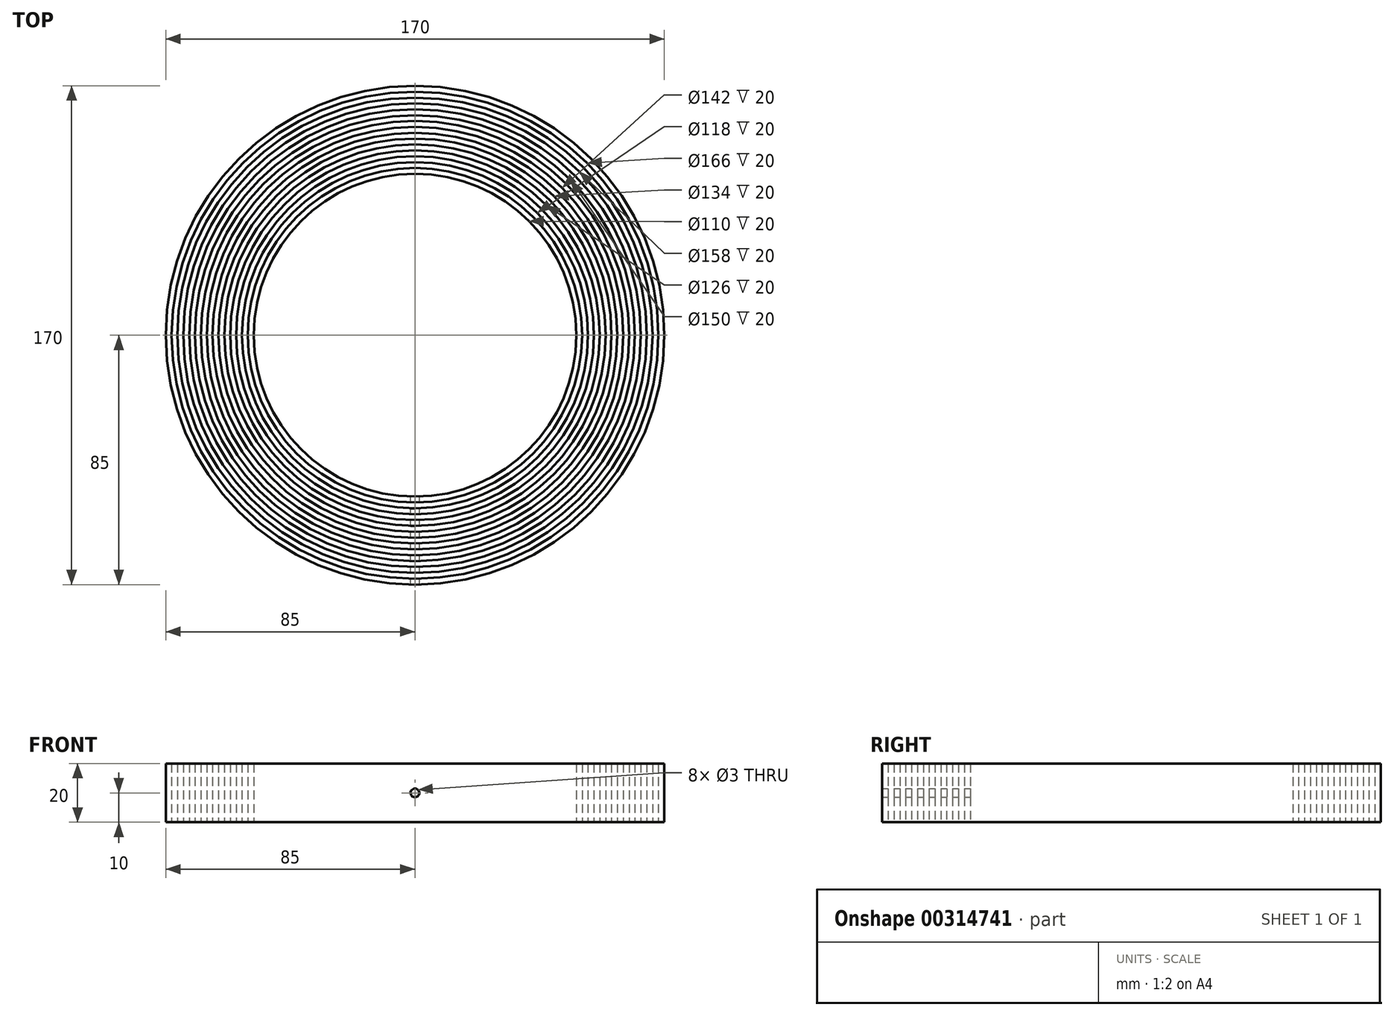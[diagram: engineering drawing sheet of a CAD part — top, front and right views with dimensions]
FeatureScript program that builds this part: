
annotation { "Feature Type Name" : "Feature", "Feature Type Description" : "" }
export const myFeature = defineFeature(function(context is Context, id is Id, definition is map)
    precondition{}
    {
        {
            var Q0;
            Q0=qCreatedBy(makeId("Top.planeOp"),FACE);
            var sketch = newSketch(context, id + "F0", { "sketchPlane" : qUnion([Q0])});
            skCircle(sketch, "E0", {"center": v(0, 0) * mm, "radius": 85 * mm});
            skCircle(sketch, "E1.0", {"center": v(0, 0) * mm, "radius": 83 * mm});
            skCircle(sketch, "E2.0", {"center": v(0, 0) * mm, "radius": 81 * mm});
            skCircle(sketch, "E3.0", {"center": v(0, 0) * mm, "radius": 79 * mm});
            skCircle(sketch, "E4.0", {"center": v(0, 0) * mm, "radius": 77 * mm});
            skCircle(sketch, "E5.0", {"center": v(0, 0) * mm, "radius": 75 * mm});
            skCircle(sketch, "E6.0", {"center": v(0, 0) * mm, "radius": 73 * mm});
            skCircle(sketch, "E7.0", {"center": v(0, 0) * mm, "radius": 71 * mm});
            skCircle(sketch, "E8.0", {"center": v(0, 0) * mm, "radius": 69 * mm});
            skCircle(sketch, "E9.0", {"center": v(0, 0) * mm, "radius": 67 * mm});
            skCircle(sketch, "E10.0", {"center": v(0, 0) * mm, "radius": 65 * mm});
            skCircle(sketch, "E11.0", {"center": v(0, 0) * mm, "radius": 63 * mm});
            skCircle(sketch, "E12.0", {"center": v(0, 0) * mm, "radius": 61 * mm});
            skCircle(sketch, "E13.0", {"center": v(0, 0) * mm, "radius": 59 * mm});
            skCircle(sketch, "E14.0", {"center": v(0, 0) * mm, "radius": 57 * mm});
            skCircle(sketch, "E15.0", {"center": v(0, 0) * mm, "radius": 55 * mm});
            skSolve(sketch);
        }
        {
            var Q0;
            Q0=makeQuery(id+"F0.imprint","IMPRINT",FACE,{"disambiguationData":[TD([[makeQuery(id+"F0.imprint","IMPRINT",EDGE,{"derivedFrom":sQuery(id+"F0.wireOp",EDGE,"E0")}),1.0]])]});
            var Q1;
            Q1=makeQuery(id+"F0.imprint","IMPRINT",FACE,{"disambiguationData":[TD([[makeQuery(id+"F0.imprint","IMPRINT",EDGE,{"derivedFrom":sQuery(id+"F0.wireOp",EDGE,"E2.0")}),1.0]])]});
            var Q2;
            Q2=makeQuery(id+"F0.imprint","IMPRINT",FACE,{"disambiguationData":[TD([[makeQuery(id+"F0.imprint","IMPRINT",EDGE,{"derivedFrom":sQuery(id+"F0.wireOp",EDGE,"E4.0")}),1.0]])]});
            var Q3;
            Q3=makeQuery(id+"F0.imprint","IMPRINT",FACE,{"disambiguationData":[TD([[makeQuery(id+"F0.imprint","IMPRINT",EDGE,{"derivedFrom":sQuery(id+"F0.wireOp",EDGE,"E6.0")}),1.0]])]});
            var Q4;
            Q4=makeQuery(id+"F0.imprint","IMPRINT",FACE,{"disambiguationData":[TD([[makeQuery(id+"F0.imprint","IMPRINT",EDGE,{"derivedFrom":sQuery(id+"F0.wireOp",EDGE,"E8.0")}),1.0]])]});
            var Q5;
            Q5=makeQuery(id+"F0.imprint","IMPRINT",FACE,{"disambiguationData":[TD([[makeQuery(id+"F0.imprint","IMPRINT",EDGE,{"derivedFrom":sQuery(id+"F0.wireOp",EDGE,"E10.0")}),1.0]])]});
            var Q6;
            Q6=makeQuery(id+"F0.imprint","IMPRINT",FACE,{"disambiguationData":[TD([[makeQuery(id+"F0.imprint","IMPRINT",EDGE,{"derivedFrom":sQuery(id+"F0.wireOp",EDGE,"E12.0")}),1.0]])]});
            var Q7;
            Q7=makeQuery(id+"F0.imprint","IMPRINT",FACE,{"disambiguationData":[TD([[makeQuery(id+"F0.imprint","IMPRINT",EDGE,{"derivedFrom":sQuery(id+"F0.wireOp",EDGE,"E14.0")}),1.0]])]});
            extrude(context, id + "F1", {"entities" : qUnion([Q0, Q1, Q2, Q3, Q4, Q5, Q6, Q7]), "depth" : 20 * mm});
        }
        {
            var Q0;
            Q0=qCreatedBy(makeId("Front.planeOp"),FACE);
            var sketch = newSketch(context, id + "F2", { "sketchPlane" : qUnion([Q0])});
            skCircle(sketch, "E16", {"center": v(0, 10) * mm, "radius": 1.5 * mm});
            skSolve(sketch);
        }
        {
            var Q0;
            Q0=sQuery(id+"F2.wireOp",VERTEX,"E16.center");
            var Q1;
            Q1=makeQuery(id+"F1.opExtrude","SWEPT_BODY",BODY,{"disambiguationData":[OSD([sQuery(id+"F0.wireOp",EDGE,"E0"),sQuery(id+"F0.wireOp",EDGE,"E1.0")])]});
            var Q2;
            Q2=makeQuery(id+"F1.opExtrude","SWEPT_BODY",BODY,{"disambiguationData":[OSD([sQuery(id+"F0.wireOp",EDGE,"E2.0"),sQuery(id+"F0.wireOp",EDGE,"E3.0")])]});
            var Q3;
            Q3=makeQuery(id+"F1.opExtrude","SWEPT_BODY",BODY,{"disambiguationData":[OSD([sQuery(id+"F0.wireOp",EDGE,"E4.0"),sQuery(id+"F0.wireOp",EDGE,"E5.0")])]});
            var Q4;
            Q4=makeQuery(id+"F1.opExtrude","SWEPT_BODY",BODY,{"disambiguationData":[OSD([sQuery(id+"F0.wireOp",EDGE,"E6.0"),sQuery(id+"F0.wireOp",EDGE,"E7.0")])]});
            var Q5;
            Q5=makeQuery(id+"F1.opExtrude","SWEPT_BODY",BODY,{"disambiguationData":[OSD([sQuery(id+"F0.wireOp",EDGE,"E8.0"),sQuery(id+"F0.wireOp",EDGE,"E9.0")])]});
            var Q6;
            Q6=makeQuery(id+"F1.opExtrude","SWEPT_BODY",BODY,{"disambiguationData":[OSD([sQuery(id+"F0.wireOp",EDGE,"E10.0"),sQuery(id+"F0.wireOp",EDGE,"E11.0")])]});
            var Q7;
            Q7=makeQuery(id+"F1.opExtrude","SWEPT_BODY",BODY,{"disambiguationData":[OSD([sQuery(id+"F0.wireOp",EDGE,"E12.0"),sQuery(id+"F0.wireOp",EDGE,"E13.0")])]});
            var Q8;
            Q8=makeQuery(id+"F1.opExtrude","SWEPT_BODY",BODY,{"disambiguationData":[OSD([sQuery(id+"F0.wireOp",EDGE,"E14.0"),sQuery(id+"F0.wireOp",EDGE,"E15.0")])]});
            hole(context, id + "F3", {"style" : HoleStyle.SIMPLE, "endStyle" : HoleEndStyle.THROUGH, "oppositeDirection" : true, "holeDiameter" : 3 * mm, "isTappedThrough" : true, "tappedDepth" : 12 * mm, "tapClearance" : 3, "locations" : qUnion([Q0]), "scope" : qUnion([Q1, Q2, Q3, Q4, Q5, Q6, Q7, Q8])});
        }
    });
